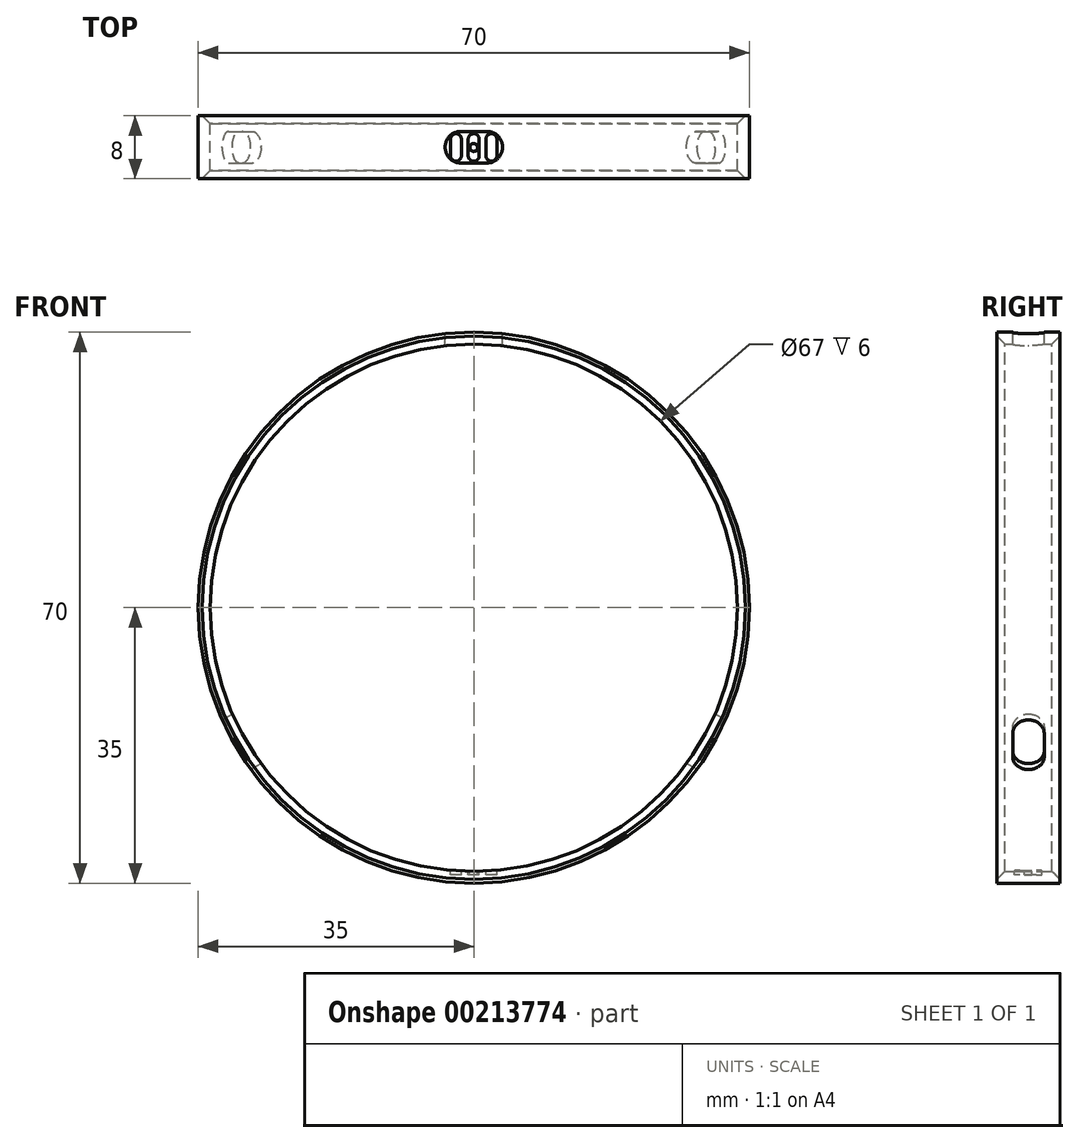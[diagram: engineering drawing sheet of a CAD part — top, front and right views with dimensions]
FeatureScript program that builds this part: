
annotation { "Feature Type Name" : "Feature", "Feature Type Description" : "" }
export const myFeature = defineFeature(function(context is Context, id is Id, definition is map)
    precondition{}
    {
        {
            var Q0;
            Q0=qCreatedBy(makeId("Front.planeOp"),FACE);
            var sketch = newSketch(context, id + "F0", { "sketchPlane" : qUnion([Q0])});
            skCircle(sketch, "E0", {"center": v(0, 0) * mm, "radius": 33.5 * mm});
            skCircle(sketch, "E1.0", {"center": v(0, 0) * mm, "radius": 35 * mm});
            skLineSegment(sketch, "E2.bottom", {"start": v(3.63, 34.81) * mm, "end": v(-3.63, 34.81) * mm, "construction": true});
            skLineSegment(sketch, "E2.top", {"start": v(3.63, 36.97) * mm, "end": v(-3.63, 36.97) * mm});
            skLineSegment(sketch, "E2.left", {"start": v(3.63, 34.81) * mm, "end": v(3.63, 36.97) * mm});
            skLineSegment(sketch, "E2.right", {"start": v(-3.63, 34.81) * mm, "end": v(-3.63, 36.97) * mm});
            skPoint(sketch, "E2.middle", {"position": v(0, 35.89) * mm});
            skLineSegment(sketch, "E3.1.0", {"start": v(-28.33, -20.55) * mm, "end": v(-30.2, -21.63) * mm});
            skLineSegment(sketch, "E3.1.1", {"start": v(-31.96, -14.26) * mm, "end": v(-33.83, -15.34) * mm});
            skLineSegment(sketch, "E3.1.2", {"start": v(-33.83, -15.34) * mm, "end": v(-30.2, -21.63) * mm});
            skLineSegment(sketch, "E3.1.3", {"start": v(-31.96, -14.26) * mm, "end": v(-28.33, -20.55) * mm, "construction": true});
            skLineSegment(sketch, "E3.2.0", {"start": v(31.96, -14.26) * mm, "end": v(33.83, -15.34) * mm});
            skLineSegment(sketch, "E3.2.1", {"start": v(28.33, -20.55) * mm, "end": v(30.2, -21.63) * mm});
            skLineSegment(sketch, "E3.2.2", {"start": v(30.2, -21.63) * mm, "end": v(33.83, -15.34) * mm});
            skLineSegment(sketch, "E3.2.3", {"start": v(28.33, -20.55) * mm, "end": v(31.96, -14.26) * mm, "construction": true});
            skLineSegment(sketch, "E4", {"start": v(0, 0) * mm, "end": v(24.75, 24.75) * mm, "construction": true});
            skLineSegment(sketch, "E5", {"start": v(0, 0) * mm, "end": v(-24.75, 24.75) * mm, "construction": true});
            skLineSegment(sketch, "E6.MirrorCS", {"start": v(0, 0) * mm, "end": v(24.75, -24.75) * mm, "construction": true});
            skLineSegment(sketch, "E7.MirrorCS", {"start": v(0, 0) * mm, "end": v(-24.75, -24.75) * mm, "construction": true});
            skLineSegment(sketch, "E8.0", {"start": v(-0.14, 0.14) * mm, "end": v(0, 0.28) * mm});
            skLineSegment(sketch, "E9.MirrorCS", {"start": v(0.14, -0.14) * mm, "end": v(0.28, 0) * mm});
            skLineSegment(sketch, "E10.MirrorCS", {"start": v(0.14, 0.14) * mm, "end": v(0, 0.28) * mm});
            skLineSegment(sketch, "E11.MirrorCS", {"start": v(-0.14, -0.14) * mm, "end": v(-0.28, 0) * mm});
            skLineSegment(sketch, "E12.MirrorCS", {"start": v(0.14, 0.14) * mm, "end": v(0.28, 0) * mm});
            skLineSegment(sketch, "E13.MirrorCS", {"start": v(-0.14, -0.14) * mm, "end": v(0, -0.28) * mm});
            skLineSegment(sketch, "E14.MirrorCS", {"start": v(0.14, -0.14) * mm, "end": v(0, -0.28) * mm});
            skLineSegment(sketch, "E15.MirrorCS", {"start": v(-0.14, 0.14) * mm, "end": v(-0.28, 0) * mm});
            skLineSegment(sketch, "E16.trimOffspring", {"start": v(-7.2, -7.48) * mm, "end": v(-23.55, -23.83) * mm, "construction": true});
            skLineSegment(sketch, "E17.trimOffspring", {"start": v(-7.48, -7.2) * mm, "end": v(-23.83, -23.55) * mm, "construction": true});
            skLineSegment(sketch, "E18.trimOffspring", {"start": v(-7.48, 7.2) * mm, "end": v(-23.83, 23.55) * mm, "construction": true});
            skLineSegment(sketch, "E19.trimOffspring", {"start": v(-7.2, 7.48) * mm, "end": v(-23.55, 23.83) * mm, "construction": true});
            skLineSegment(sketch, "E20.trimOffspring", {"start": v(7.2, 7.48) * mm, "end": v(23.55, 23.83) * mm, "construction": true});
            skLineSegment(sketch, "E21.trimOffspring", {"start": v(7.48, 7.2) * mm, "end": v(23.83, 23.55) * mm, "construction": true});
            skLineSegment(sketch, "E22.trimOffspring", {"start": v(7.2, -7.48) * mm, "end": v(23.55, -23.83) * mm, "construction": true});
            skLineSegment(sketch, "E23.trimOffspring", {"start": v(7.48, -7.2) * mm, "end": v(23.83, -23.55) * mm, "construction": true});
            skLineSegment(sketch, "E24", {"start": v(-3.63, 34.81) * mm, "end": v(-3.63, 31.7) * mm});
            skLineSegment(sketch, "E25", {"start": v(-3.63, 31.7) * mm, "end": v(3.63, 31.7) * mm});
            skLineSegment(sketch, "E26", {"start": v(3.63, 31.7) * mm, "end": v(3.63, 34.81) * mm});
            skLineSegment(sketch, "E27", {"start": v(31.96, -14.26) * mm, "end": v(7.27, 0) * mm});
            skLineSegment(sketch, "E28", {"start": v(28.33, -20.55) * mm, "end": v(3.35, -6.13) * mm});
            skLineSegment(sketch, "E29", {"start": v(3.35, -6.13) * mm, "end": v(7.27, 0) * mm});
            skLineSegment(sketch, "E30", {"start": v(-28.33, -20.55) * mm, "end": v(-3.28, -6.1) * mm});
            skLineSegment(sketch, "E31", {"start": v(-31.96, -14.26) * mm, "end": v(-6.86, 0.24) * mm});
            skLineSegment(sketch, "E32", {"start": v(-6.86, 0.24) * mm, "end": v(-3.28, -6.1) * mm});
            skLineSegment(sketch, "E33", {"start": v(0, -0.28) * mm, "end": v(0, 35) * mm, "construction": true});
            skLineSegment(sketch, "E34", {"start": v(0.28, 0) * mm, "end": v(-20.96, 28.03) * mm});
            skLineSegment(sketch, "E35.MirrorCS", {"start": v(-0.28, 0) * mm, "end": v(20.96, 28.03) * mm});
            skSolve(sketch);
        }
        {
            var Q0;
            Q0=makeQuery(id+"F0.imprint","IMPRINT",FACE,{"disambiguationData":[TD([[makeQuery(id+"F0.imprint","IMPRINT",EDGE,{"derivedFrom":sQuery(id+"F0.wireOp",EDGE,"E0")}),-1.0]])]});
            var Q1;
            {var subQ2=sQuery(id+"F0.wireOp",EDGE,"E16.trimOffspring");var subQ7=sQuery(id+"F0.wireOp",EDGE,"E0");var subQ9=makeQuery(id+"F0.imprint","INTERSECT",VERTEX,{"derivedFrom":[subQ7,subQ2]});Q1=makeQuery(id+"F0.imprint","IMPRINT",FACE,{"disambiguationData":[TD([[makeQuery(id+"F0.imprint","IMPRINT",EDGE,{"disambiguationData":[TD([[subQ9,-1.0]])],"derivedFrom":subQ7}),-1.0]])]});}
            var Q2;
            {var subQ5=sQuery(id+"F0.wireOp",EDGE,"E21.trimOffspring");var subQ7=sQuery(id+"F0.wireOp",EDGE,"E0");var subQ8=makeQuery(id+"F0.imprint","INTERSECT",VERTEX,{"derivedFrom":[subQ7,subQ5]});Q2=makeQuery(id+"F0.imprint","IMPRINT",FACE,{"disambiguationData":[TD([[makeQuery(id+"F0.imprint","IMPRINT",EDGE,{"disambiguationData":[TD([[subQ8,1.0]])],"derivedFrom":subQ7}),-1.0]])]});}
            var Q3;
            {var subQ2=sQuery(id+"F0.wireOp",EDGE,"E19.trimOffspring");var subQ7=sQuery(id+"F0.wireOp",EDGE,"E0");var subQ8=makeQuery(id+"F0.imprint","INTERSECT",VERTEX,{"derivedFrom":[subQ7,subQ2]});Q3=makeQuery(id+"F0.imprint","IMPRINT",FACE,{"disambiguationData":[TD([[makeQuery(id+"F0.imprint","IMPRINT",EDGE,{"disambiguationData":[TD([[subQ8,1.0]])],"derivedFrom":subQ7}),-1.0]])]});}
            var Q4;
            {var subQ5=sQuery(id+"F0.wireOp",EDGE,"E17.trimOffspring");var subQ6=sQuery(id+"F0.wireOp",EDGE,"E0");var subQ7=makeQuery(id+"F0.imprint","INTERSECT",VERTEX,{"derivedFrom":[subQ6,subQ5]});Q4=makeQuery(id+"F0.imprint","IMPRINT",FACE,{"disambiguationData":[TD([[makeQuery(id+"F0.imprint","IMPRINT",EDGE,{"disambiguationData":[TD([[subQ7,1.0]])],"derivedFrom":subQ6}),-1.0]])]});}
            extrude(context, id + "F1", {"entities" : qUnion([Q0, Q1, Q2, Q3, Q4]), "depth" : 4 * mm, "hasSecondDirection" : true, "secondDirectionOppositeDirection" : true, "secondDirectionDepth" : 4 * mm});
        }
        {
            var Q0;
            Q0=makeQuery(id+"F1.opExtrude","CAP_EDGE",EDGE,{"disambiguationData":[OSD([sQuery(id+"F0.wireOp",EDGE,"E0")])],"isStart":false});
            var Q1;
            Q1=makeQuery(id+"F1.opExtrude","CAP_EDGE",EDGE,{"disambiguationData":[OSD([sQuery(id+"F0.wireOp",EDGE,"E0")])],"isStart":true});
            chamfer(context, id + "F2", {"entities" : qUnion([Q0, Q1]), "width" : 1 * mm, "tangentPropagation" : true});
        }
        {
            var Q0;
            Q0=qCreatedBy(makeId("Top.planeOp"),FACE);
            var sketch = newSketch(context, id + "F3", { "sketchPlane" : qUnion([Q0])});
            skCircle(sketch, "E36", {"center": v(0, 0) * mm, "radius": 0.15 * mm});
            skCircle(sketch, "E37.1.0.0", {"center": v(0, -0.6) * mm, "radius": 0.15 * mm});
            skCircle(sketch, "E37.2.0.0", {"center": v(0, -1.2) * mm, "radius": 0.15 * mm});
            skCircle(sketch, "E37.3.0.0", {"center": v(0, -1.8) * mm, "radius": 0.15 * mm});
            skCircle(sketch, "E37.4.0.0", {"center": v(0, -2.4) * mm, "radius": 0.15 * mm});
            skCircle(sketch, "E37.5.0.0", {"center": v(0, -3) * mm, "radius": 0.15 * mm});
            skCircle(sketch, "E37.6.0.0", {"center": v(0, -3.6) * mm, "radius": 0.15 * mm});
            skLineSegment(sketch, "E37.direction1", {"start": v(0, 0) * mm, "end": v(0, -0.6) * mm, "construction": true});
            skCircle(sketch, "E38.MirrorC", {"center": v(0, 0.6) * mm, "radius": 0.15 * mm});
            skCircle(sketch, "E39.MirrorC", {"center": v(0, 1.2) * mm, "radius": 0.15 * mm});
            skCircle(sketch, "E40.MirrorC", {"center": v(0, 1.8) * mm, "radius": 0.15 * mm});
            skCircle(sketch, "E41.MirrorC", {"center": v(0, 2.4) * mm, "radius": 0.15 * mm});
            skCircle(sketch, "E42.MirrorC", {"center": v(0, 3) * mm, "radius": 0.15 * mm});
            skCircle(sketch, "E43.MirrorC", {"center": v(0, 3.6) * mm, "radius": 0.15 * mm});
            skSolve(sketch);
        }
        {
            var Q0;
            Q0=makeQuery(id+"F0.imprint","IMPRINT",FACE,{"disambiguationData":[TD([[makeQuery(id+"F0.imprint","IMPRINT",EDGE,{"derivedFrom":sQuery(id+"F0.wireOp",EDGE,"E2.top")}),1.0]])]});
            var Q1;
            {var subQ0=sQuery(id+"F0.wireOp",EDGE,"E24");var subQ1=sQuery(id+"F0.wireOp",EDGE,"E0");var subQ2=makeQuery(id+"F0.imprint","INTERSECT",VERTEX,{"derivedFrom":[subQ1,subQ0]});Q1=makeQuery(id+"F0.imprint","IMPRINT",FACE,{"disambiguationData":[TD([[makeQuery(id+"F0.imprint","IMPRINT",EDGE,{"disambiguationData":[TD([[subQ2,1.0]])],"derivedFrom":subQ1}),-1.0]])]});}
            var Q2;
            {var subQ5=sQuery(id+"F0.wireOp",EDGE,"E25");Q2=makeQuery(id+"F0.imprint","IMPRINT",FACE,{"disambiguationData":[TD([[makeQuery(id+"F0.imprint","IMPRINT",EDGE,{"derivedFrom":subQ5}),1.0]])]});}
            var Q3;
            {var subQ5=sQuery(id+"F0.wireOp",EDGE,"E29");Q3=makeQuery(id+"F0.imprint","IMPRINT",FACE,{"disambiguationData":[TD([[makeQuery(id+"F0.imprint","IMPRINT",EDGE,{"derivedFrom":subQ5}),-1.0]])]});}
            var Q4;
            {var subQ0=sQuery(id+"F0.wireOp",EDGE,"E28");var subQ1=sQuery(id+"F0.wireOp",EDGE,"E0");var subQ2=makeQuery(id+"F0.imprint","INTERSECT",VERTEX,{"derivedFrom":[subQ1,subQ0]});Q4=makeQuery(id+"F0.imprint","IMPRINT",FACE,{"disambiguationData":[TD([[makeQuery(id+"F0.imprint","IMPRINT",EDGE,{"disambiguationData":[TD([[subQ2,-1.0]])],"derivedFrom":subQ1}),-1.0]])]});}
            var Q5;
            {var subQ0=sQuery(id+"F0.wireOp",EDGE,"E3.2.0");Q5=makeQuery(id+"F0.imprint","IMPRINT",FACE,{"disambiguationData":[TD([[makeQuery(id+"F0.imprint","IMPRINT",EDGE,{"derivedFrom":subQ0}),-1.0]])]});}
            var Q6;
            {var subQ5=sQuery(id+"F0.wireOp",EDGE,"E32");Q6=makeQuery(id+"F0.imprint","IMPRINT",FACE,{"disambiguationData":[TD([[makeQuery(id+"F0.imprint","IMPRINT",EDGE,{"derivedFrom":subQ5}),-1.0]])]});}
            var Q7;
            {var subQ0=sQuery(id+"F0.wireOp",EDGE,"E3.1.0");Q7=makeQuery(id+"F0.imprint","IMPRINT",FACE,{"disambiguationData":[TD([[makeQuery(id+"F0.imprint","IMPRINT",EDGE,{"derivedFrom":subQ0}),-1.0]])]});}
            var Q8;
            {var subQ0=sQuery(id+"F0.wireOp",EDGE,"E31");var subQ1=sQuery(id+"F0.wireOp",EDGE,"E0");var subQ2=makeQuery(id+"F0.imprint","INTERSECT",VERTEX,{"derivedFrom":[subQ1,subQ0]});Q8=makeQuery(id+"F0.imprint","IMPRINT",FACE,{"disambiguationData":[TD([[makeQuery(id+"F0.imprint","IMPRINT",EDGE,{"disambiguationData":[TD([[subQ2,-1.0]])],"derivedFrom":subQ1}),-1.0]])]});}
            extrude(context, id + "F4", {"entities" : qUnion([Q0, Q1, Q2, Q3, Q4, Q5, Q6, Q7, Q8]), "operationType" : NewBodyOperationType.REMOVE, "oppositeDirection" : true, "depth" : 2 * mm, "hasSecondDirection" : true, "secondDirectionOppositeDirection" : false, "secondDirectionDepth" : 2 * mm});
        }
        {
            var Q0;
            Q0=makeQuery(id+"F4.boolean.opBoolean","COPY",EDGE,{"derivedFrom":makeQuery(id+"F4.opExtrude","CAP_EDGE",EDGE,{"disambiguationData":[OSD([sQuery(id+"F0.wireOp",EDGE,"E3.2.1"),sQuery(id+"F0.wireOp",EDGE,"E28")])],"isStart":false})});
            var Q1;
            Q1=makeQuery(id+"F4.boolean.opBoolean","COPY",EDGE,{"derivedFrom":makeQuery(id+"F4.opExtrude","CAP_EDGE",EDGE,{"disambiguationData":[OSD([sQuery(id+"F0.wireOp",EDGE,"E3.2.0"),sQuery(id+"F0.wireOp",EDGE,"E27")])],"isStart":false})});
            var Q2;
            Q2=makeQuery(id+"F4.boolean.opBoolean","COPY",EDGE,{"derivedFrom":makeQuery(id+"F4.opExtrude","CAP_EDGE",EDGE,{"disambiguationData":[OSD([sQuery(id+"F0.wireOp",EDGE,"E3.2.0"),sQuery(id+"F0.wireOp",EDGE,"E27")])],"isStart":true})});
            var Q3;
            Q3=makeQuery(id+"F4.boolean.opBoolean","COPY",EDGE,{"derivedFrom":makeQuery(id+"F4.opExtrude","CAP_EDGE",EDGE,{"disambiguationData":[OSD([sQuery(id+"F0.wireOp",EDGE,"E3.2.1"),sQuery(id+"F0.wireOp",EDGE,"E28")])],"isStart":true})});
            var Q4;
            Q4=makeQuery(id+"F4.boolean.opBoolean","COPY",EDGE,{"derivedFrom":makeQuery(id+"F4.opExtrude","CAP_EDGE",EDGE,{"disambiguationData":[OSD([sQuery(id+"F0.wireOp",EDGE,"E3.1.0"),sQuery(id+"F0.wireOp",EDGE,"E30")])],"isStart":false})});
            var Q5;
            Q5=makeQuery(id+"F4.boolean.opBoolean","COPY",EDGE,{"derivedFrom":makeQuery(id+"F4.opExtrude","CAP_EDGE",EDGE,{"disambiguationData":[OSD([sQuery(id+"F0.wireOp",EDGE,"E3.1.1"),sQuery(id+"F0.wireOp",EDGE,"E31")])],"isStart":false})});
            var Q6;
            Q6=makeQuery(id+"F4.boolean.opBoolean","COPY",EDGE,{"derivedFrom":makeQuery(id+"F4.opExtrude","CAP_EDGE",EDGE,{"disambiguationData":[OSD([sQuery(id+"F0.wireOp",EDGE,"E3.1.1"),sQuery(id+"F0.wireOp",EDGE,"E31")])],"isStart":true})});
            var Q7;
            Q7=makeQuery(id+"F4.boolean.opBoolean","COPY",EDGE,{"derivedFrom":makeQuery(id+"F4.opExtrude","CAP_EDGE",EDGE,{"disambiguationData":[OSD([sQuery(id+"F0.wireOp",EDGE,"E3.1.0"),sQuery(id+"F0.wireOp",EDGE,"E30")])],"isStart":true})});
            var Q8;
            Q8=makeQuery(id+"F4.boolean.opBoolean","COPY",EDGE,{"derivedFrom":makeQuery(id+"F4.opExtrude","CAP_EDGE",EDGE,{"disambiguationData":[OSD([sQuery(id+"F0.wireOp",EDGE,"E2.right"),sQuery(id+"F0.wireOp",EDGE,"E24")])],"isStart":false})});
            var Q9;
            Q9=makeQuery(id+"F4.boolean.opBoolean","COPY",EDGE,{"derivedFrom":makeQuery(id+"F4.opExtrude","CAP_EDGE",EDGE,{"disambiguationData":[OSD([sQuery(id+"F0.wireOp",EDGE,"E2.left"),sQuery(id+"F0.wireOp",EDGE,"E26")])],"isStart":false})});
            var Q10;
            Q10=makeQuery(id+"F4.boolean.opBoolean","COPY",EDGE,{"derivedFrom":makeQuery(id+"F4.opExtrude","CAP_EDGE",EDGE,{"disambiguationData":[OSD([sQuery(id+"F0.wireOp",EDGE,"E2.right"),sQuery(id+"F0.wireOp",EDGE,"E24")])],"isStart":true})});
            var Q11;
            Q11=makeQuery(id+"F4.boolean.opBoolean","COPY",EDGE,{"derivedFrom":makeQuery(id+"F4.opExtrude","CAP_EDGE",EDGE,{"disambiguationData":[OSD([sQuery(id+"F0.wireOp",EDGE,"E2.left"),sQuery(id+"F0.wireOp",EDGE,"E26")])],"isStart":true})});
            fillet(context, id + "F5", {"entities" : qUnion([Q0, Q1, Q2, Q3, Q4, Q5, Q6, Q7, Q8, Q9, Q10, Q11]), "radius" : 1.94 * mm, "tangentPropagation" : true, "allowEdgeOverflow" : false});
        }
        {
            var Q0;
            Q0=qCreatedBy(makeId("Top.planeOp"),FACE);
            var sketch = newSketch(context, id + "F6", { "sketchPlane" : qUnion([Q0])});
            skLineSegment(sketch, "E44.bottom", {"start": v(-0.71, 1.01) * mm, "end": v(-0.71, -1.08) * mm});
            skArc(sketch, "E45.filletArc", {"start": v(0.69, 1.01) * mm, "mid": v(0.48, 1.5) * mm, "end": v(-0.01, 1.71) * mm});
            skArc(sketch, "E46.filletArc", {"start": v(-0.01, 1.71) * mm, "mid": v(-0.5, 1.5) * mm, "end": v(-0.71, 1.01) * mm});
            skArc(sketch, "E47.filletArc", {"start": v(-0.01, -1.78) * mm, "mid": v(0.48, -1.57) * mm, "end": v(0.69, -1.08) * mm});
            skArc(sketch, "E48.filletArc", {"start": v(-0.71, -1.08) * mm, "mid": v(-0.5, -1.57) * mm, "end": v(-0.01, -1.78) * mm});
            skLineSegment(sketch, "E49.bottom", {"start": v(-2.97, 1.01) * mm, "end": v(-2.97, -1.08) * mm});
            skLineSegment(sketch, "E49.top", {"start": v(-1.57, 1.01) * mm, "end": v(-1.57, -1.08) * mm});
            skArc(sketch, "E50.filletArc", {"start": v(-1.57, 1.01) * mm, "mid": v(-1.77, 1.5) * mm, "end": v(-2.27, 1.71) * mm});
            skArc(sketch, "E51.filletArc", {"start": v(-2.27, 1.71) * mm, "mid": v(-2.76, 1.5) * mm, "end": v(-2.97, 1.01) * mm});
            skArc(sketch, "E52.filletArc", {"start": v(-2.27, -1.78) * mm, "mid": v(-1.77, -1.57) * mm, "end": v(-1.57, -1.08) * mm});
            skArc(sketch, "E53.filletArc", {"start": v(-2.97, -1.08) * mm, "mid": v(-2.76, -1.57) * mm, "end": v(-2.27, -1.78) * mm});
            skLineSegment(sketch, "E54", {"start": v(0.69, 1.01) * mm, "end": v(0.69, -1.08) * mm});
            skCircle(sketch, "E55", {"center": v(-0.01, -0.04) * mm, "radius": 0.5 * mm});
            skLineSegment(sketch, "E56.bottom", {"start": v(1.54, 1.01) * mm, "end": v(1.54, -1.08) * mm});
            skLineSegment(sketch, "E56.top", {"start": v(2.94, 1.01) * mm, "end": v(2.94, -1.08) * mm});
            skArc(sketch, "E57.filletArc", {"start": v(2.94, 1.01) * mm, "mid": v(2.74, 1.5) * mm, "end": v(2.24, 1.71) * mm});
            skArc(sketch, "E58.filletArc", {"start": v(2.24, 1.71) * mm, "mid": v(1.75, 1.5) * mm, "end": v(1.54, 1.01) * mm});
            skArc(sketch, "E59.filletArc", {"start": v(2.24, -1.78) * mm, "mid": v(2.74, -1.57) * mm, "end": v(2.94, -1.08) * mm});
            skArc(sketch, "E60.filletArc", {"start": v(1.54, -1.08) * mm, "mid": v(1.75, -1.57) * mm, "end": v(2.24, -1.78) * mm});
            skSolve(sketch);
        }
        {
            var Q0;
            Q0=makeQuery(id+"F6.imprint","IMPRINT",FACE,{"disambiguationData":[TD([[makeQuery(id+"F6.imprint","IMPRINT",EDGE,{"derivedFrom":sQuery(id+"F6.wireOp",EDGE,"E49.bottom")}),1.0]])]});
            var Q1;
            Q1=makeQuery(id+"F6.imprint","IMPRINT",FACE,{"disambiguationData":[TD([[makeQuery(id+"F6.imprint","IMPRINT",EDGE,{"derivedFrom":sQuery(id+"F6.wireOp",EDGE,"E44.bottom")}),1.0]])]});
            var Q2;
            Q2=makeQuery(id+"F6.imprint","IMPRINT",FACE,{"disambiguationData":[TD([[makeQuery(id+"F6.imprint","IMPRINT",EDGE,{"derivedFrom":sQuery(id+"F6.wireOp",EDGE,"E56.bottom")}),1.0]])]});
            extrude(context, id + "F7", {"entities" : qUnion([Q0, Q1, Q2]), "operationType" : NewBodyOperationType.REMOVE, "oppositeDirection" : true, "depth" : 33.93 * mm, "offsetDistance" : 25 * mm});
        }
    });
